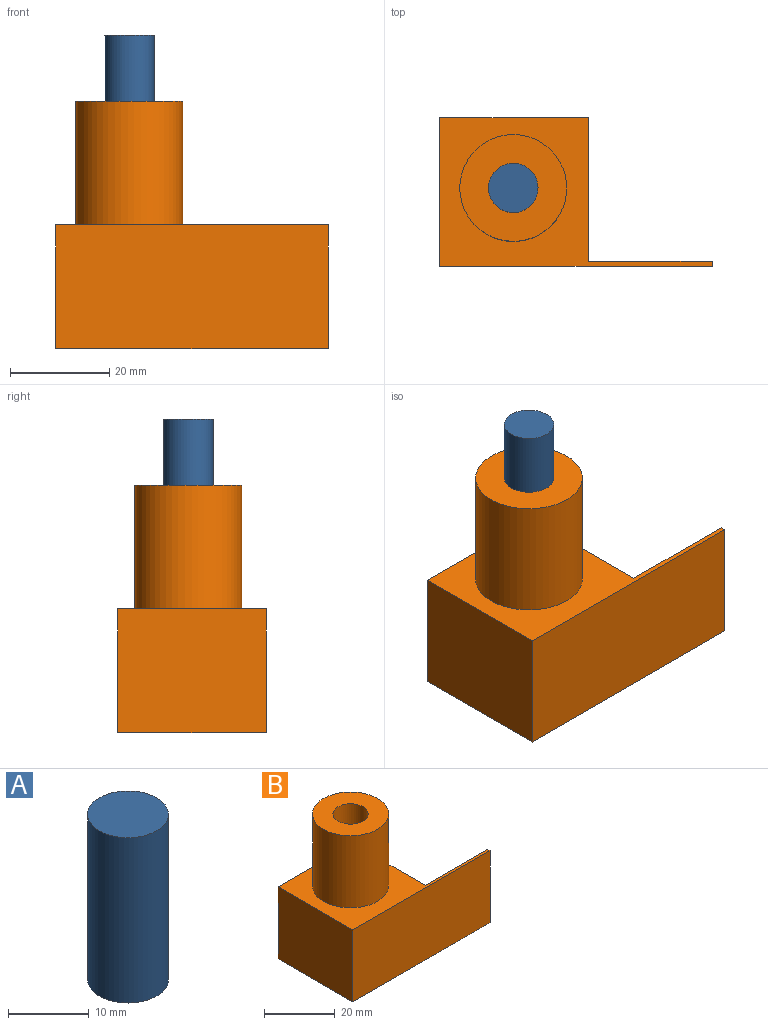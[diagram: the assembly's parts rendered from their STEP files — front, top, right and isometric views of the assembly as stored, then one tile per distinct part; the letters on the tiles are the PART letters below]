
ASSEMBLY  parts=2 mates=1
PART A: 3 faces, bbox 10x10x25 mm
  f0: cylinder r=5mm len=25mm, axis (0,0,-1), area 785.4mm2, adj f1,f2
  f1: plane 10x10mm, normal (0,0,1), area 78.5mm2, adj f0
  f2: plane 10x10mm, normal (0,0,-1), area 78.5mm2, adj f0
PART B: 12 faces, bbox 55x30x50 mm
  f0: plane 30x25mm, normal (-1,0,0), area 750mm2, adj f1,f3,f4,f5
  f1: plane 55x25mm, normal (0,-1,0), area 1375mm2, adj f0,f4,f5,f8
  f2: plane 29x25mm, normal (1,0,0), area 725mm2, adj f3,f4,f5,f9
  f3: plane 30x25mm, normal (0,1,0), area 750mm2, adj f0,f2,f4,f5
  f4: plane 55x30mm, normal (0,0,1), area 560.1mm2, adj f0,f1,f2,f3,f6,f8,f9
  f5: plane 55x30mm, normal (0,0,-1), area 925mm2, adj f0,f1,f2,f3,f8,f9
  f6: cylinder r=10.78mm len=25mm, axis (0,0,-1), area 1693mm2, adj f4,f7
  f7: plane 21.56x21.56mm, normal (0,0,1), area 286.4mm2, adj f6,f10
  f8: plane 25x1mm, normal (1,0,0), area 25mm2, adj f1,f4,f5,f9
  f9: plane 25x25mm, normal (0,1,0), area 625mm2, adj f2,f4,f5,f8
  f10: cylinder r=5mm len=25mm, axis (0,0,1), area 785.4mm2, adj f7,f11
  f11: plane 10x10mm, normal (0,0,1), area 78.5mm2, adj f10
PLACE A t=(0,0,0.77)mm
PLACE B t=(-7.2,-2.03,0.2)mm fixed
MATE slider B.f6 <-> A.f0  axis (0,0,1) through (7.63,13.72,50.2)mm
